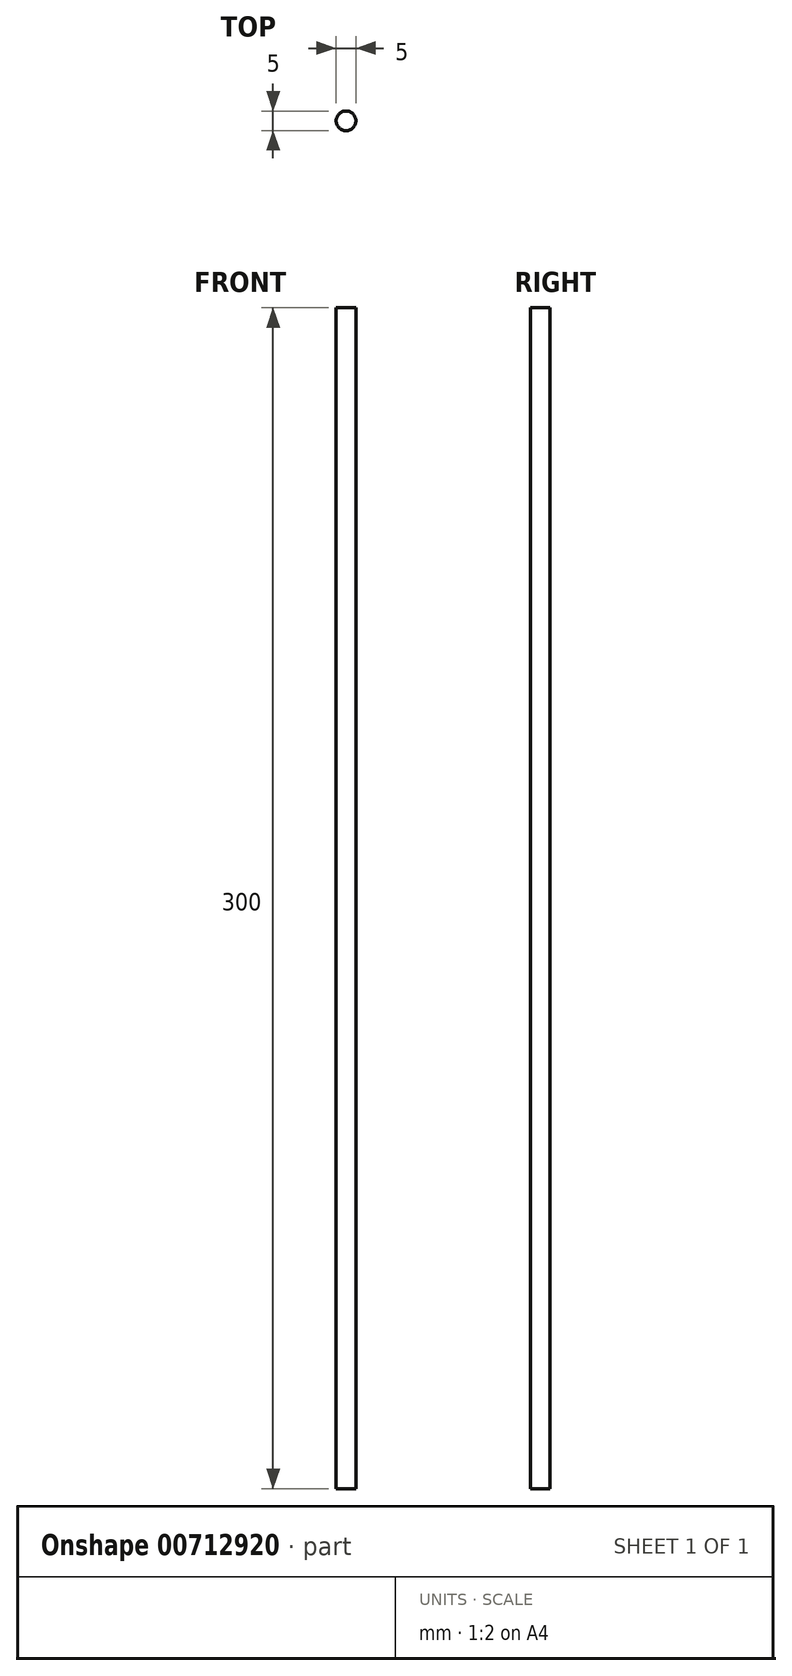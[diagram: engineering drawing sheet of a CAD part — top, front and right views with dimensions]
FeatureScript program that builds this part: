
annotation { "Feature Type Name" : "Feature", "Feature Type Description" : "" }
export const myFeature = defineFeature(function(context is Context, id is Id, definition is map)
    precondition{}
    {
        {
            var Q0;
            Q0=qCreatedBy(makeId("Top.planeOp"),FACE);
            var sketch = newSketch(context, id + "F0", { "sketchPlane" : qUnion([Q0])});
            skCircle(sketch, "E0", {"center": v(0, 0) * mm, "radius": 2.5 * mm});
            skSolve(sketch);
        }
        {
            var Q0;
            Q0=makeQuery(id+"F0.imprint","IMPRINT",FACE,{"disambiguationData":[TD([[makeQuery(id+"F0.imprint","IMPRINT",EDGE,{"derivedFrom":sQuery(id+"F0.wireOp",EDGE,"E0")}),1.0]])]});
            extrude(context, id + "F1", {"entities" : qUnion([Q0]), "depth" : 300 * mm, "offsetDistance" : 25 * mm});
        }
    });
